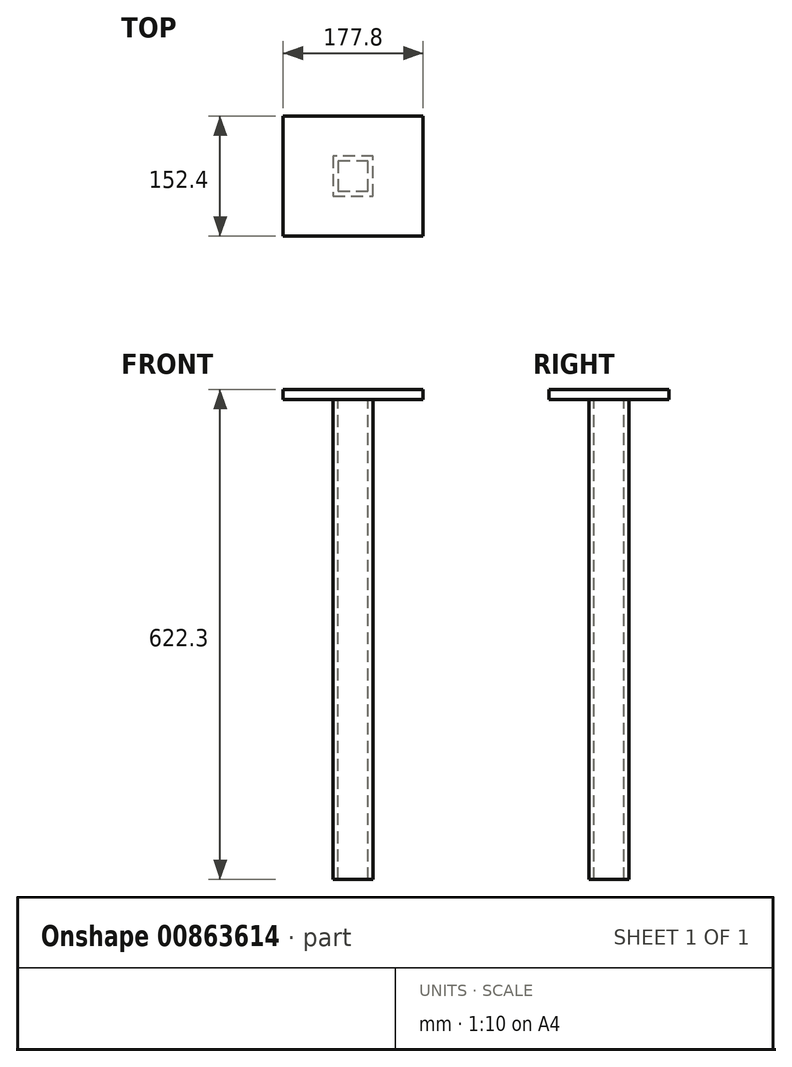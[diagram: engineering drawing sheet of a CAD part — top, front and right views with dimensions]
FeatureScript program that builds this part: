
annotation { "Feature Type Name" : "Feature", "Feature Type Description" : "" }
export const myFeature = defineFeature(function(context is Context, id is Id, definition is map)
    precondition{}
    {
        {
            var Q0;
            Q0=qCreatedBy(makeId("Top.planeOp"),FACE);
            var sketch = newSketch(context, id + "F0", { "sketchPlane" : qUnion([Q0])});
            skLineSegment(sketch, "E0.bottom", {"start": v(0, 0) * mm, "end": v(177.8, 0) * mm});
            skLineSegment(sketch, "E0.top", {"start": v(0, 152.4) * mm, "end": v(177.8, 152.4) * mm});
            skLineSegment(sketch, "E0.left", {"start": v(0, 0) * mm, "end": v(0, 152.4) * mm});
            skLineSegment(sketch, "E0.right", {"start": v(177.8, 0) * mm, "end": v(177.8, 152.4) * mm});
            skSolve(sketch);
        }
        {
            var Q0;
            Q0 = qSketchRegion(id + "F0", true);
            extrude(context, id + "F1", {"entities" : qUnion([Q0]), "depth" : 12.7 * mm, "offsetDistance" : 25.4 * mm});
        }
        {
            var Q0;
            Q0=makeQuery(id+"F1.opExtrude","CAP_FACE",FACE,{"disambiguationData":[OSD([sQuery(id+"F0.wireOp",EDGE,"E0.bottom"),sQuery(id+"F0.wireOp",EDGE,"E0.top"),sQuery(id+"F0.wireOp",EDGE,"E0.left"),sQuery(id+"F0.wireOp",EDGE,"E0.right")])],"isStart":true});
            var sketch = newSketch(context, id + "F2", { "sketchPlane" : qUnion([Q0])});
            skLineSegment(sketch, "E1", {"start": v(63.5, -50.8) * mm, "end": v(114.3, -50.8) * mm});
            skLineSegment(sketch, "E2", {"start": v(114.3, -50.8) * mm, "end": v(114.3, -101.6) * mm});
            skLineSegment(sketch, "E3", {"start": v(114.3, -101.6) * mm, "end": v(63.5, -101.6) * mm});
            skLineSegment(sketch, "E4", {"start": v(63.5, -101.6) * mm, "end": v(63.5, -50.8) * mm});
            skLineSegment(sketch, "E5", {"start": v(69.85, -57.15) * mm, "end": v(107.95, -57.15) * mm});
            skLineSegment(sketch, "E6", {"start": v(107.95, -57.15) * mm, "end": v(107.95, -95.25) * mm});
            skLineSegment(sketch, "E7", {"start": v(107.95, -95.25) * mm, "end": v(69.85, -95.25) * mm});
            skLineSegment(sketch, "E8", {"start": v(69.85, -95.25) * mm, "end": v(69.85, -57.15) * mm});
            skSolve(sketch);
        }
        {
            var Q0;
            Q0 = qSketchRegion(id + "F2", true);
            extrude(context, id + "F3", {"entities" : qUnion([Q0]), "operationType" : NewBodyOperationType.ADD, "depth" : 609.6 * mm, "offsetDistance" : 25.4 * mm});
        }
    });
